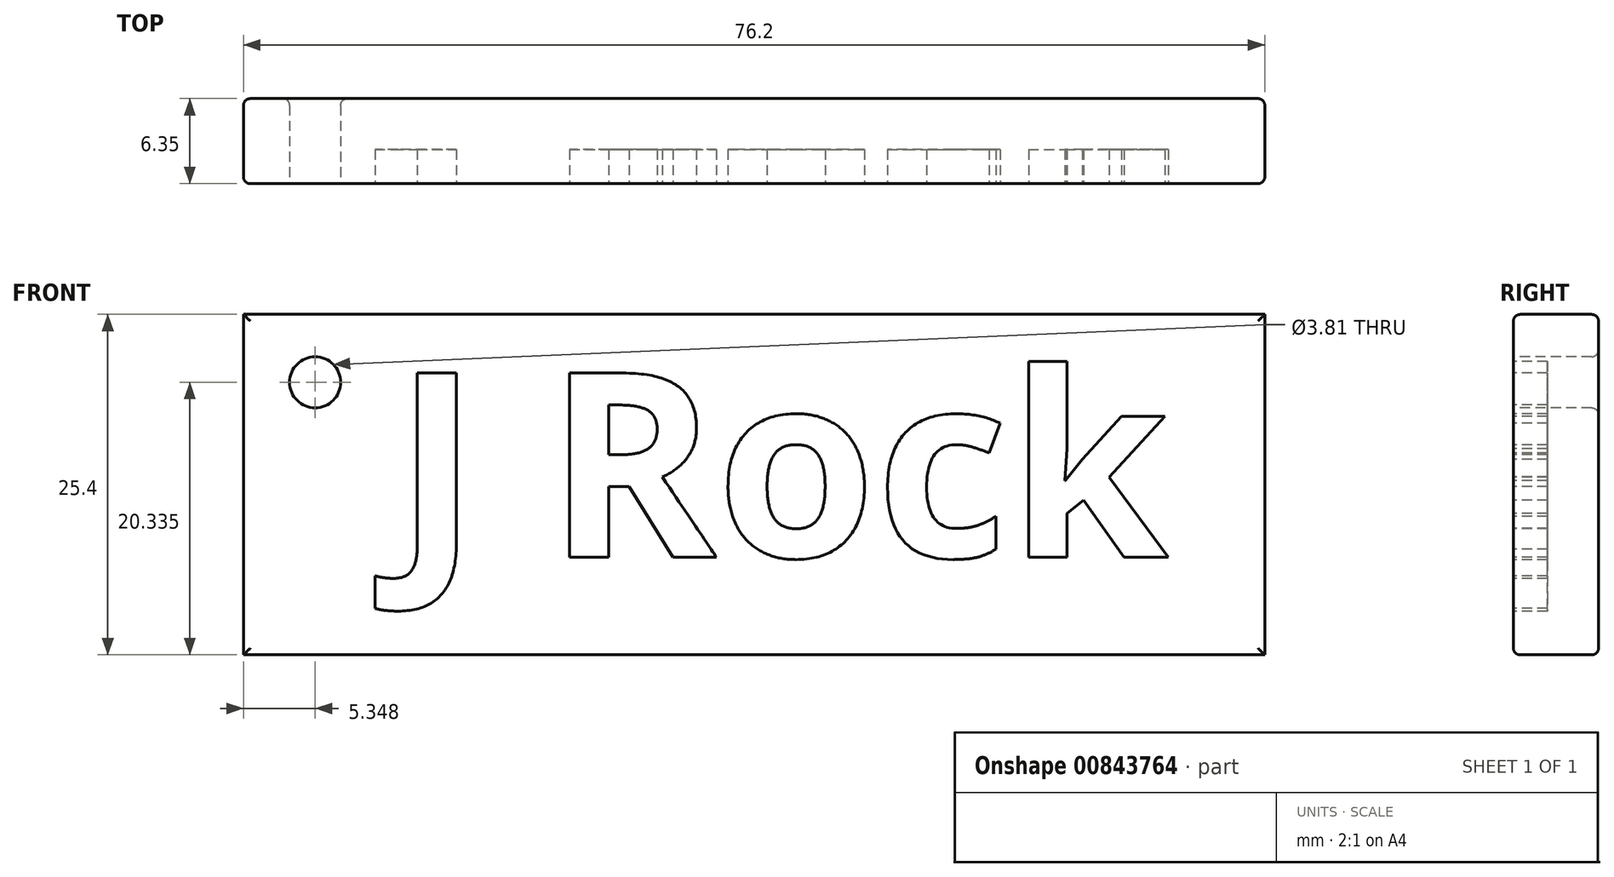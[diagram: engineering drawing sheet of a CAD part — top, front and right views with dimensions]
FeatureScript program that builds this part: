
annotation { "Feature Type Name" : "Feature", "Feature Type Description" : "" }
export const myFeature = defineFeature(function(context is Context, id is Id, definition is map)
    precondition{}
    {
        {
            var Q0;
            Q0=qCreatedBy(makeId("Front.planeOp"),FACE);
            var sketch = newSketch(context, id + "F0", { "sketchPlane" : qUnion([Q0])});
            skLineSegment(sketch, "E0.bottom", {"start": v(-38.1, 12.7) * mm, "end": v(38.1, 12.7) * mm});
            skLineSegment(sketch, "E0.top", {"start": v(-38.1, -12.7) * mm, "end": v(38.1, -12.7) * mm});
            skLineSegment(sketch, "E0.left", {"start": v(-38.1, 12.7) * mm, "end": v(-38.1, -12.7) * mm});
            skLineSegment(sketch, "E0.right", {"start": v(38.1, 12.7) * mm, "end": v(38.1, -12.7) * mm});
            skPoint(sketch, "E0.middle", {"position": v(0, 0) * mm});
            skSolve(sketch);
        }
        {
            var Q0;
            Q0 = qSketchRegion(id + "F0", true);
            extrude(context, id + "F1", {"entities" : qUnion([Q0]), "depth" : 6.35 * mm, "offsetDistance" : 25.4 * mm});
        }
        {
            var Q0;
            {var subQ0=sQuery(id+"F0.wireOp",EDGE,"E0.left");var subQ1=sQuery(id+"F0.wireOp",EDGE,"E0.bottom");var subQ2=sQuery(id+"F0.wireOp",EDGE,"E0.right");var subQ3=sQuery(id+"F0.wireOp",EDGE,"E0.top");Q0=makeQuery(id+"Fu403jQB54a9aeW_1.boolean.opBoolean","SPLIT",FACE,{"disambiguationData":[TD([makeQuery(id+"F1.opExtrude","SWEPT_FACE",FACE,{"disambiguationData":[OSD([subQ1])]})])],"derivedFrom":makeQuery(id+"F1.opExtrude","CAP_FACE",FACE,{"disambiguationData":[OSD([subQ1,subQ3,subQ0,subQ2])],"isStart":false})});}
            var sketch = newSketch(context, id + "F2", { "sketchPlane" : qUnion([Q0])});
            skCircle(sketch, "E1", {"center": v(-32.75, 7.63) * mm, "radius": 1.9 * mm});
            skSolve(sketch);
        }
        {
            var Q0;
            Q0 = qSketchRegion(id + "F2", true);
            extrude(context, id + "F3", {"entities" : qUnion([Q0]), "operationType" : NewBodyOperationType.REMOVE, "oppositeDirection" : true, "depth" : 25.4 * mm, "offsetDistance" : 25.4 * mm});
        }
        {
            var Q0;
            Q0=makeQuery(id+"F1.opExtrude","CAP_EDGE",EDGE,{"disambiguationData":[OSD([sQuery(id+"F0.wireOp",EDGE,"E0.bottom")])],"isStart":false});
            var Q1;
            Q1=makeQuery(id+"F1.opExtrude","CAP_EDGE",EDGE,{"disambiguationData":[OSD([sQuery(id+"F0.wireOp",EDGE,"E0.right")])],"isStart":false});
            var Q2;
            Q2=makeQuery(id+"F1.opExtrude","CAP_EDGE",EDGE,{"disambiguationData":[OSD([sQuery(id+"F0.wireOp",EDGE,"E0.left")])],"isStart":false});
            var Q3;
            Q3=makeQuery(id+"F1.opExtrude","CAP_EDGE",EDGE,{"disambiguationData":[OSD([sQuery(id+"F0.wireOp",EDGE,"E0.top")])],"isStart":false});
            var Q4;
            Q4=makeQuery(id+"F3.boolean.opBoolean","COPY",EDGE,{"derivedFrom":makeQuery(id+"F3.opExtrude","CAP_EDGE",EDGE,{"disambiguationData":[OSD([sQuery(id+"F2.wireOp",EDGE,"E1")])],"isStart":true})});
            var Q5;
            Q5=makeQuery(id+"F3.boolean.opBoolean","INTERSECT",EDGE,{"derivedFrom":[makeQuery(id+"F1.opExtrude","CAP_FACE",FACE,{"disambiguationData":[OSD([sQuery(id+"F0.wireOp",EDGE,"E0.bottom"),sQuery(id+"F0.wireOp",EDGE,"E0.top"),sQuery(id+"F0.wireOp",EDGE,"E0.left"),sQuery(id+"F0.wireOp",EDGE,"E0.right")])],"isStart":true}),makeQuery(id+"F3.opExtrude","SWEPT_FACE",FACE,{"disambiguationData":[OSD([sQuery(id+"F2.wireOp",EDGE,"E1")])]})]});
            var Q6;
            Q6=makeQuery(id+"F1.opExtrude","CAP_EDGE",EDGE,{"disambiguationData":[OSD([sQuery(id+"F0.wireOp",EDGE,"E0.bottom")])],"isStart":true});
            var Q7;
            Q7=makeQuery(id+"F1.opExtrude","CAP_EDGE",EDGE,{"disambiguationData":[OSD([sQuery(id+"F0.wireOp",EDGE,"E0.left")])],"isStart":true});
            var Q8;
            Q8=makeQuery(id+"F1.opExtrude","CAP_EDGE",EDGE,{"disambiguationData":[OSD([sQuery(id+"F0.wireOp",EDGE,"E0.top")])],"isStart":true});
            var Q9;
            Q9=makeQuery(id+"F1.opExtrude","CAP_EDGE",EDGE,{"disambiguationData":[OSD([sQuery(id+"F0.wireOp",EDGE,"E0.right")])],"isStart":true});
            fillet(context, id + "F4", {"entities" : qUnion([Q0, Q1, Q2, Q3, Q4, Q5, Q6, Q7, Q8, Q9]), "radius" : 0.5 * mm, "tangentPropagation" : true, "allowEdgeOverflow" : false});
        }
        {
            var Q0;
            Q0=makeQuery(id+"F1.opExtrude","CAP_FACE",FACE,{"disambiguationData":[OSD([sQuery(id+"F0.wireOp",EDGE,"E0.bottom"),sQuery(id+"F0.wireOp",EDGE,"E0.top"),sQuery(id+"F0.wireOp",EDGE,"E0.left"),sQuery(id+"F0.wireOp",EDGE,"E0.right")])],"isStart":false});
            var sketch = newSketch(context, id + "F5", { "sketchPlane" : qUnion([Q0])});
            skText(sketch, "E2", { "text": "J Rock ", "fontName": "OpenSans-Bold.ttf"});
            const initialGuessF5  = {"E2": [-0.02686, -0.0054, 1, 0, 0.01384]};
            skSetInitialGuess(sketch, initialGuessF5);
            skSolve(sketch);
        }
        {
            var Q0;
            Q0 = qSketchRegion(id + "F5", true);
            extrude(context, id + "F6", {"entities" : qUnion([Q0]), "operationType" : NewBodyOperationType.REMOVE, "oppositeDirection" : true, "depth" : 2.54 * mm, "offsetDistance" : 25.4 * mm});
        }
    });
